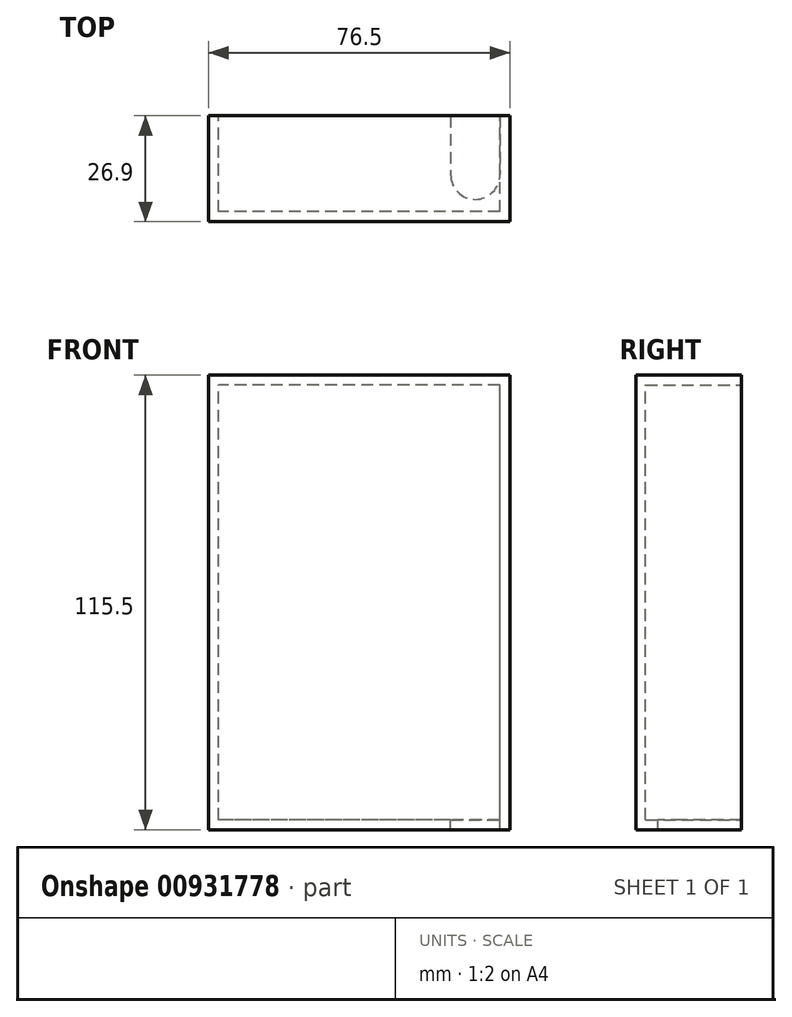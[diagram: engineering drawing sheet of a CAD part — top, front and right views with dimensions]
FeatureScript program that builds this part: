
annotation { "Feature Type Name" : "Feature", "Feature Type Description" : "" }
export const myFeature = defineFeature(function(context is Context, id is Id, definition is map)
    precondition{}
    {
        {
            var Q0;
            Q0=qCreatedBy(makeId("Front.planeOp"),FACE);
            var sketch = newSketch(context, id + "F0", { "sketchPlane" : qUnion([Q0])});
            skLineSegment(sketch, "E0.bottom", {"start": v(38.25, -57.75) * mm, "end": v(-38.25, -57.75) * mm});
            skLineSegment(sketch, "E0.top", {"start": v(38.25, 57.75) * mm, "end": v(-38.25, 57.75) * mm});
            skLineSegment(sketch, "E0.left", {"start": v(38.25, -57.75) * mm, "end": v(38.25, 57.75) * mm});
            skLineSegment(sketch, "E0.right", {"start": v(-38.25, -57.75) * mm, "end": v(-38.25, 57.75) * mm});
            skPoint(sketch, "E0.middle", {"position": v(0, 0) * mm});
            skSolve(sketch);
        }
        {
            var Q0;
            Q0 = qSketchRegion(id + "F0", true);
            extrude(context, id + "F1", {"entities" : qUnion([Q0]), "depth" : 26.9 * mm, "offsetDistance" : 25 * mm});
        }
        {
            var Q0;
            Q0=makeQuery(id+"F1.opExtrude","CAP_FACE",FACE,{"disambiguationData":[OSD([sQuery(id+"F0.wireOp",EDGE,"E0.bottom"),sQuery(id+"F0.wireOp",EDGE,"E0.top"),sQuery(id+"F0.wireOp",EDGE,"E0.left"),sQuery(id+"F0.wireOp",EDGE,"E0.right")])],"isStart":true});
            shell(context, id + "F2", {"entities" : qUnion([Q0]), "thickness" : 2.5 * mm});
        }
        {
            var Q0;
            Q0=makeQuery(id+"F2.opShell","OFFSET_FACE",FACE,{"disambiguationData":[OSD([sQuery(id+"F0.wireOp",EDGE,"E0.bottom")])]});
            var sketch = newSketch(context, id + "F3", { "sketchPlane" : qUnion([Q0])});
            skLineSegment(sketch, "E1.bottom", {"start": v(35.75, 0) * mm, "end": v(23.25, 0) * mm});
            skLineSegment(sketch, "E1.left", {"start": v(35.75, 0) * mm, "end": v(35.75, -15) * mm});
            skLineSegment(sketch, "E1.right", {"start": v(23.25, 0) * mm, "end": v(23.25, -15) * mm});
            skPoint(sketch, "E2.visualSharp", {"position": v(23.25, -20) * mm});
            skPoint(sketch, "E3.visualSharp", {"position": v(35.75, -20) * mm});
            skArc(sketch, "E4", {"start": v(23.25, -15) * mm, "mid": v(29.5, -21.25) * mm, "end": v(35.75, -15) * mm});
            skSolve(sketch);
        }
        {
            var Q0;
            Q0=makeQuery(id+"F3.imprint","IMPRINT",FACE,{"disambiguationData":[TD([[makeQuery(id+"F3.imprint","IMPRINT",EDGE,{"derivedFrom":sQuery(id+"F3.wireOp",EDGE,"E1.bottom")}),1.0]])]});
            extrude(context, id + "F4", {"entities" : qUnion([Q0]), "operationType" : NewBodyOperationType.REMOVE, "oppositeDirection" : true, "depth" : 25 * mm, "offsetDistance" : 25 * mm});
        }
    });
